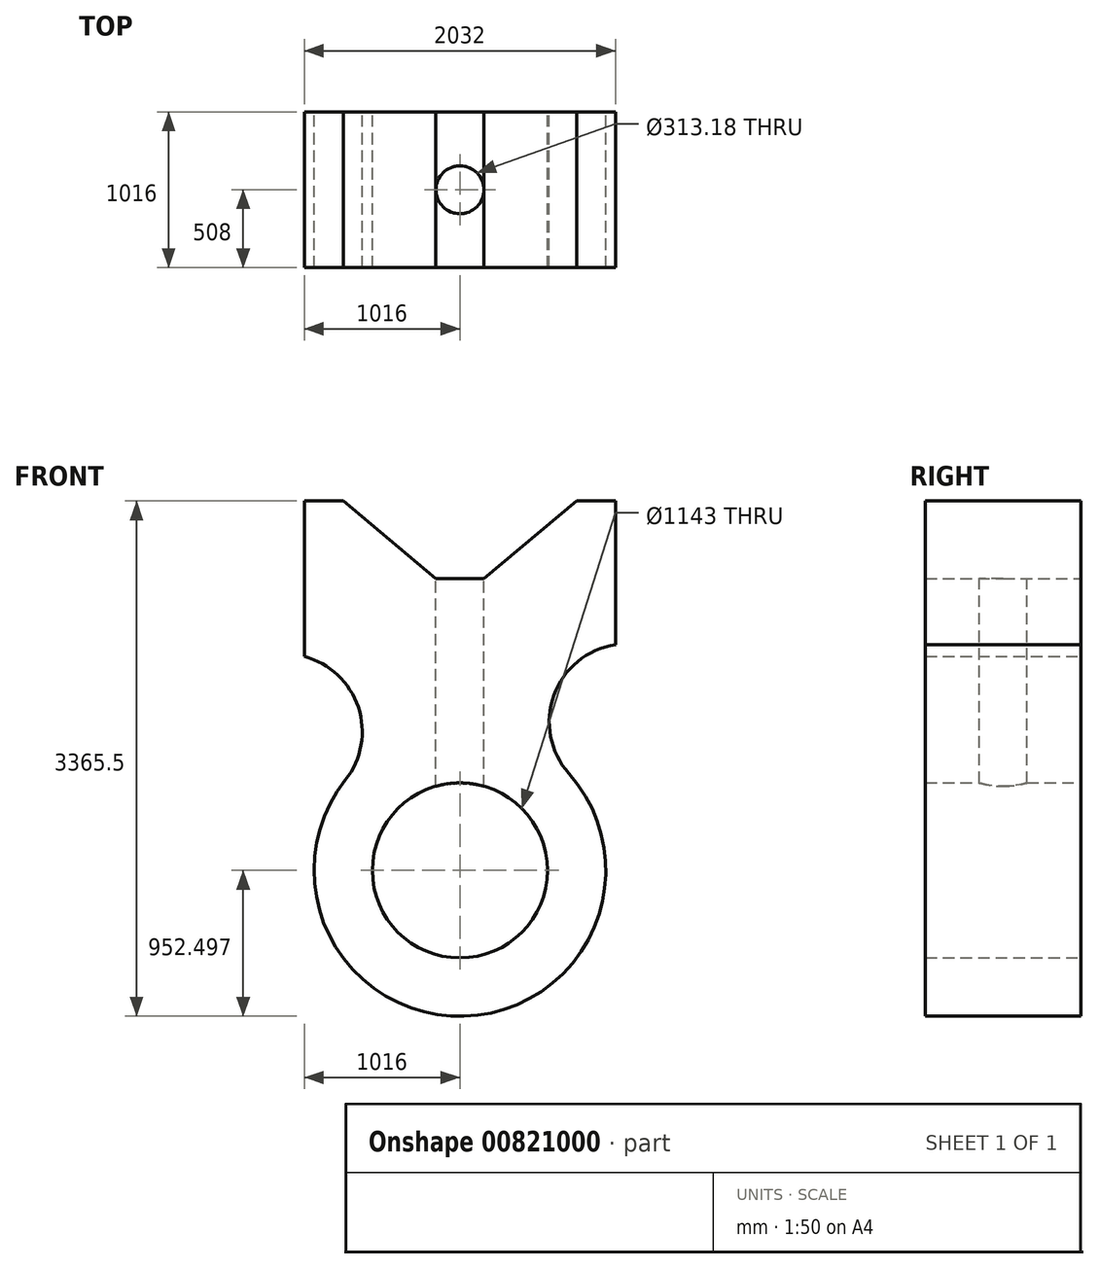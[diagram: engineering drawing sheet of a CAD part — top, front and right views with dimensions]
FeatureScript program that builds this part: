
annotation { "Feature Type Name" : "Feature", "Feature Type Description" : "" }
export const myFeature = defineFeature(function(context is Context, id is Id, definition is map)
    precondition{}
    {
        {
            var Q0;
            Q0=qCreatedBy(makeId("Front.planeOp"),FACE);
            var sketch = newSketch(context, id + "F0", { "sketchPlane" : qUnion([Q0])});
            skLineSegment(sketch, "E0", {"start": v(129.66, -76.4) * mm, "end": v(129.66, 939.6) * mm});
            skLineSegment(sketch, "E1", {"start": v(129.66, 939.6) * mm, "end": v(383.66, 939.6) * mm});
            skLineSegment(sketch, "E2", {"start": v(2161.66, 939.6) * mm, "end": v(2161.66, 0) * mm});
            skLineSegment(sketch, "E3", {"start": v(1145.66, 431.6) * mm, "end": v(1145.66, -1473.4) * mm});
            skLineSegment(sketch, "E4", {"start": v(2161.66, 939.6) * mm, "end": v(1907.66, 939.6) * mm});
            skArc(sketch, "E5", {"start": v(2161.66, 0) * mm, "mid": v(1759.06, -329.35) * mm, "end": v(1857.19, -840.16) * mm});
            skArc(sketch, "E6", {"start": v(398.5, -882.64) * mm, "mid": v(481.92, -406.88) * mm, "end": v(129.66, -76.4) * mm});
            skCircle(sketch, "E7", {"center": v(1145.66, -1473.4) * mm, "radius": 571.5 * mm});
            skCircle(sketch, "E8", {"center": v(1145.66, -1473.4) * mm, "radius": 952.5 * mm});
            skLineSegment(sketch, "E9", {"start": v(1145.66, -1473.4) * mm, "end": v(0, -567.57) * mm});
            skLineSegment(sketch, "E10", {"start": v(1145.66, -1473.4) * mm, "end": v(2236.67, -502.43) * mm});
            skLineSegment(sketch, "E11", {"start": v(989.07, 431.6) * mm, "end": v(383.66, 939.6) * mm});
            skLineSegment(sketch, "E12", {"start": v(1302.25, 431.6) * mm, "end": v(1907.66, 939.6) * mm});
            skLineSegment(sketch, "E13", {"start": v(989.07, 431.6) * mm, "end": v(1302.25, 431.6) * mm});
            skLineSegment(sketch, "E14.trimOffspring", {"start": v(1907.66, 939.6) * mm, "end": v(2161.66, 939.6) * mm});
            skPoint(sketch, "E15.orphan", {"position": v(1145.66, 939.6) * mm});
            skSolve(sketch);
        }
        {
            var Q0;
            Q0=makeQuery(id+"F0.imprint","IMPRINT",FACE,{"disambiguationData":[TD([[makeQuery(id+"F0.imprint","IMPRINT",EDGE,{"derivedFrom":sQuery(id+"F0.wireOp",EDGE,"E0")}),-1.0]])]});
            var Q1;
            Q1=makeQuery(id+"F0.imprint","IMPRINT",FACE,{"disambiguationData":[TD([[makeQuery(id+"F0.imprint","IMPRINT",EDGE,{"derivedFrom":sQuery(id+"F0.wireOp",EDGE,"E2")}),-1.0]])]});
            var Q2;
            {var subQ0=sQuery(id+"F0.wireOp",EDGE,"E8");var subQ1=sQuery(id+"F0.wireOp",EDGE,"E3");var subQ2=makeQuery(id+"F0.imprint","INTERSECT",VERTEX,{"derivedFrom":[subQ1,subQ0]});Q2=makeQuery(id+"F0.imprint","IMPRINT",FACE,{"disambiguationData":[TD([[makeQuery(id+"F0.imprint","IMPRINT",EDGE,{"disambiguationData":[TD([[subQ2,-1.0]])],"derivedFrom":subQ1}),1.0]])]});}
            var Q3;
            {var subQ0=sQuery(id+"F0.wireOp",EDGE,"E8");var subQ1=sQuery(id+"F0.wireOp",EDGE,"E3");var subQ2=makeQuery(id+"F0.imprint","INTERSECT",VERTEX,{"derivedFrom":[subQ1,subQ0]});Q3=makeQuery(id+"F0.imprint","IMPRINT",FACE,{"disambiguationData":[TD([[makeQuery(id+"F0.imprint","IMPRINT",EDGE,{"disambiguationData":[TD([[subQ2,-1.0]])],"derivedFrom":subQ1}),-1.0]])]});}
            var Q4;
            {var subQ0=sQuery(id+"F0.wireOp",EDGE,"E10");var subQ1=sQuery(id+"F0.wireOp",EDGE,"E7");var subQ2=makeQuery(id+"F0.imprint","INTERSECT",VERTEX,{"derivedFrom":[subQ1,subQ0]});Q4=makeQuery(id+"F0.imprint","IMPRINT",FACE,{"disambiguationData":[TD([[makeQuery(id+"F0.imprint","IMPRINT",EDGE,{"disambiguationData":[TD([[subQ2,1.0]])],"derivedFrom":subQ1}),-1.0]])]});}
            extrude(context, id + "F1", {"entities" : qUnion([Q0, Q1, Q2, Q3, Q4]), "depth" : 1016 * mm, "offsetDistance" : 25.4 * mm});
        }
        {
            var Q0;
            Q0=makeQuery(id+"F1.opExtrude","SWEPT_FACE",FACE,{"disambiguationData":[OSD([sQuery(id+"F0.wireOp",EDGE,"E13")])]});
            var sketch = newSketch(context, id + "F2", { "sketchPlane" : qUnion([Q0])});
            skCircle(sketch, "E16", {"center": v(1145.66, -508) * mm, "radius": 156.59 * mm});
            skPoint(sketch, "E16.centerSnap0", {"position": v(1145.66, -1016) * mm});
            skPoint(sketch, "E16.centerSnap1", {"position": v(989.07, -508) * mm});
            skSolve(sketch);
        }
        {
            var Q0;
            Q0 = qSketchRegion(id + "F2", true);
            extrude(context, id + "F3", {"entities" : qUnion([Q0]), "operationType" : NewBodyOperationType.REMOVE, "endBound" : BoundingType.UP_TO_NEXT, "oppositeDirection" : true, "depth" : 25.4 * mm, "offsetDistance" : 25.4 * mm});
        }
    });
